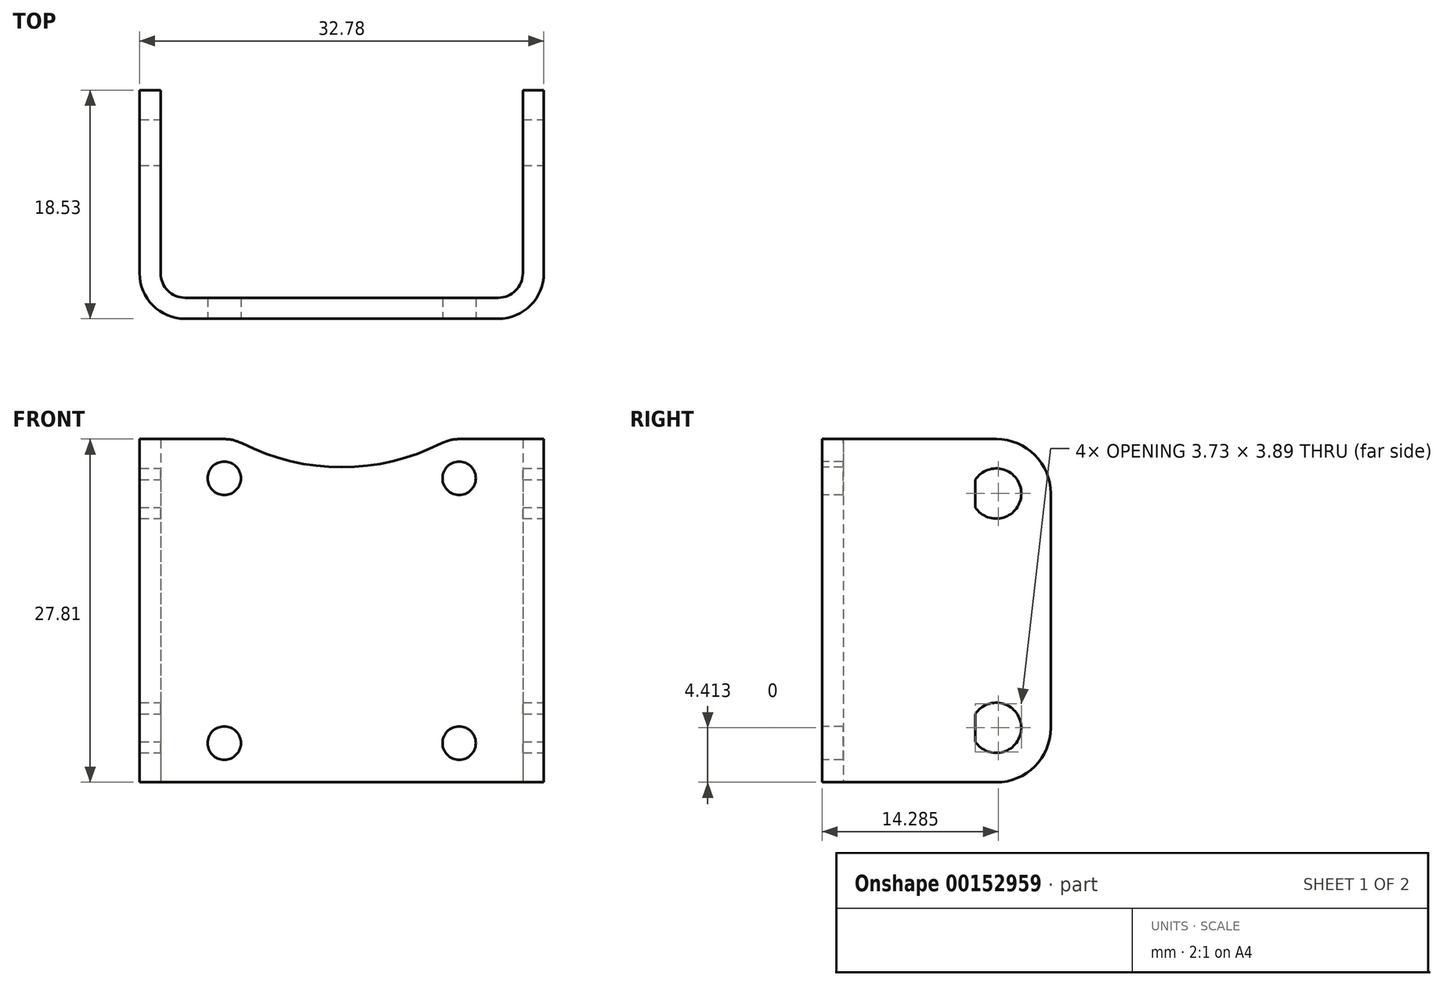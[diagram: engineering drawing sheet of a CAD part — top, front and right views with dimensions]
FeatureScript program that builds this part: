
annotation { "Feature Type Name" : "Feature", "Feature Type Description" : "" }
export const myFeature = defineFeature(function(context is Context, id is Id, definition is map)
    precondition{}
    {
        {
            var Q0;
            Q0=qCreatedBy(makeId("Top.planeOp"),FACE);
            var sketch = newSketch(context, id + "F0", { "sketchPlane" : qUnion([Q0])});
            skLineSegment(sketch, "E0.bottom", {"start": v(0, 0) * mm, "end": v(-29.36, 0) * mm});
            skLineSegment(sketch, "E0.top", {"start": v(1.7, -1.7) * mm, "end": v(-31.07, -1.7) * mm});
            skLineSegment(sketch, "E1.top", {"start": v(-29.36, 16.82) * mm, "end": v(-31.07, 16.82) * mm});
            skLineSegment(sketch, "E1.left", {"start": v(-29.36, 0) * mm, "end": v(-29.36, 16.82) * mm});
            skLineSegment(sketch, "E1.right", {"start": v(-31.07, -1.7) * mm, "end": v(-31.07, 16.82) * mm});
            skLineSegment(sketch, "E2.top", {"start": v(0, 16.82) * mm, "end": v(1.7, 16.82) * mm});
            skLineSegment(sketch, "E2.left", {"start": v(0, 0) * mm, "end": v(0, 16.82) * mm});
            skLineSegment(sketch, "E2.right", {"start": v(1.7, -1.7) * mm, "end": v(1.7, 16.82) * mm});
            skLineSegment(sketch, "E3", {"start": v(-14.68, 0) * mm, "end": v(-14.68, -1.7) * mm, "construction": true});
            skArc(sketch, "E4", {"start": v(-1.98, 0) * mm, "mid": v(-0.58, 0.58) * mm, "end": v(0, 1.98) * mm, "construction": true});
            skSolve(sketch);
        }
        {
            var Q0;
            Q0=qSketchRegion(id+"F0",true);
            extrude(context, id + "F1", {"entities" : qUnion([Q0]), "depth" : 27.8 * mm});
        }
        {
            var Q0;
            Q0=makeQuery(id+"F1.opExtrude","SWEPT_EDGE",EDGE,{"disambiguationData":[OSD([sQuery(id+"F0.wireOp",EDGE,"E0.top"),sQuery(id+"F0.wireOp",EDGE,"E2.right")])]});
            var Q1;
            Q1=makeQuery(id+"F1.opExtrude","SWEPT_EDGE",EDGE,{"disambiguationData":[OSD([sQuery(id+"F0.wireOp",EDGE,"E0.top"),sQuery(id+"F0.wireOp",EDGE,"E1.right")])]});
            var Q2;
            Q2=makeQuery(id+"FqNnmMD7oaRdpTN_1.opExtrude","CAP_EDGE",EDGE,{"disambiguationData":[OSD([sQuery(id+"FY5sMr6MULj5lJw_1.wireOp",EDGE,"W42EfhJi-fDm4-L9BW-folL-irsYfDskuzBk.top")])],"isStart":false});
            fillet(context, id + "F2", {"entities" : qUnion([Q0, Q1, Q2]), "radius" : 3.7 * mm, "tangentPropagation" : true, "allowEdgeOverflow" : false});
        }
        {
            var Q0;
            Q0=makeQuery(id+"F1.opExtrude","SWEPT_EDGE",EDGE,{"disambiguationData":[OSD([sQuery(id+"F0.wireOp",EDGE,"E0.bottom"),sQuery(id+"F0.wireOp",EDGE,"E2.left")])]});
            var Q1;
            Q1=makeQuery(id+"F1.opExtrude","SWEPT_EDGE",EDGE,{"disambiguationData":[OSD([sQuery(id+"F0.wireOp",EDGE,"E0.bottom"),sQuery(id+"F0.wireOp",EDGE,"E1.left")])]});
            fillet(context, id + "F3", {"entities" : qUnion([Q0, Q1]), "radius" : 1.98 * mm, "tangentPropagation" : true, "allowEdgeOverflow" : false});
        }
        {
            var Q0;
            Q0=makeQuery(id+"F1.opExtrude","SWEPT_FACE",FACE,{"disambiguationData":[OSD([sQuery(id+"F0.wireOp",EDGE,"E2.right")])]});
            var sketch = newSketch(context, id + "F4", { "sketchPlane" : qUnion([Q0])});
            skArc(sketch, "E5", {"start": v(10.71, 22.28) * mm, "mid": v(14.44, 23.4) * mm, "end": v(10.71, 24.52) * mm});
            skLineSegment(sketch, "E6", {"start": v(10.71, 22.28) * mm, "end": v(10.71, 24.52) * mm});
            skCircle(sketch, "E7", {"center": v(12.4, 23.4) * mm, "radius": 0.9 * mm, "construction": true});
            skArc(sketch, "E8", {"start": v(10.71, 3.3) * mm, "mid": v(14.44, 4.41) * mm, "end": v(10.71, 5.54) * mm});
            skLineSegment(sketch, "E9", {"start": v(10.71, 3.3) * mm, "end": v(10.71, 5.54) * mm});
            skLineSegment(sketch, "E10", {"start": v(12.4, 23.4) * mm, "end": v(11.5, 23.4) * mm, "construction": true});
            skLineSegment(sketch, "E11", {"start": v(12.4, 23.4) * mm, "end": v(12.4, 22.5) * mm, "construction": true});
            skLineSegment(sketch, "E12", {"start": v(11.5, 23.4) * mm, "end": v(10.71, 23.4) * mm, "construction": true});
            skLineSegment(sketch, "E13", {"start": v(12.4, 22.5) * mm, "end": v(12.4, 21.37) * mm, "construction": true});
            skLineSegment(sketch, "E14", {"start": v(12.4, 23.4) * mm, "end": v(12.4, 27.81) * mm, "construction": true});
            skLineSegment(sketch, "E15.bottom", {"start": v(12.4, 0) * mm, "end": v(16.82, 0) * mm, "construction": true});
            skLineSegment(sketch, "E15.top", {"start": v(12.4, 4.41) * mm, "end": v(16.82, 4.41) * mm, "construction": true});
            skLineSegment(sketch, "E15.left", {"start": v(12.4, 0) * mm, "end": v(12.4, 4.41) * mm, "construction": true});
            skLineSegment(sketch, "E15.right", {"start": v(16.82, 0) * mm, "end": v(16.82, 4.41) * mm, "construction": true});
            skSolve(sketch);
        }
        {
            var Q0;
            Q0=qSketchRegion(id+"F4",true);
            var Q1;
            Q1=makeQuery(id+"F1.opExtrude","SWEPT_FACE",FACE,{"disambiguationData":[OSD([sQuery(id+"F0.wireOp",EDGE,"E1.right")])]});
            extrude(context, id + "F5", {"entities" : qUnion([Q0]), "operationType" : NewBodyOperationType.REMOVE, "endBound" : BoundingType.UP_TO_SURFACE, "oppositeDirection" : true, "endBoundEntityFace" : qUnion([Q1]), "depth" : 25.4 * mm});
        }
        {
            var Q0;
            Q0=makeQuery(id+"F1.opExtrude","SWEPT_FACE",FACE,{"disambiguationData":[OSD([sQuery(id+"F0.wireOp",EDGE,"E0.top")])]});
            var sketch = newSketch(context, id + "F6", { "sketchPlane" : qUnion([Q0])});
            skArc(sketch, "E16", {"start": v(-5.16, 27.81) * mm, "mid": v(-5.9, 27.73) * mm, "end": v(-6.6, 27.47) * mm});
            skArc(sketch, "E17", {"start": v(-22.77, 27.47) * mm, "mid": v(-23.46, 27.73) * mm, "end": v(-24.2, 27.81) * mm});
            skArc(sketch, "E18", {"start": v(-22.77, 27.47) * mm, "mid": v(-14.68, 25.53) * mm, "end": v(-6.6, 27.47) * mm});
            skLineSegment(sketch, "E19", {"start": v(-24.2, 27.81) * mm, "end": v(-5.16, 27.81) * mm});
            skCircle(sketch, "E20", {"center": v(-24.2, 24.64) * mm, "radius": 1.35 * mm});
            skCircle(sketch, "E21", {"center": v(-5.16, 24.64) * mm, "radius": 1.35 * mm});
            skLineSegment(sketch, "E22", {"start": v(-14.68, 0) * mm, "end": v(-14.68, 3.18) * mm, "construction": true});
            skLineSegment(sketch, "E23", {"start": v(-24.2, 3.18) * mm, "end": v(-5.16, 3.18) * mm, "construction": true});
            skLineSegment(sketch, "E24", {"start": v(-5.16, 3.18) * mm, "end": v(-1.98, 3.18) * mm, "construction": true});
            skCircle(sketch, "E25", {"center": v(-24.2, 3.18) * mm, "radius": 1.35 * mm});
            skCircle(sketch, "E26", {"center": v(-5.16, 3.18) * mm, "radius": 1.35 * mm});
            skSolve(sketch);
        }
        {
            var Q0;
            Q0 = qSketchRegion(id + "F6", true);
            var Q1;
            Q1=makeQuery(id+"F1.opExtrude","SWEPT_FACE",FACE,{"disambiguationData":[OSD([sQuery(id+"F0.wireOp",EDGE,"E0.bottom")])]});
            extrude(context, id + "F7", {"entities" : qUnion([Q0]), "operationType" : NewBodyOperationType.REMOVE, "endBound" : BoundingType.UP_TO_SURFACE, "oppositeDirection" : true, "endBoundEntityFace" : qUnion([Q1]), "depth" : 25.4 * mm});
        }
        {
            var Q0;
            Q0=makeQuery(id+"F1.opExtrude","CAP_EDGE",EDGE,{"disambiguationData":[OSD([sQuery(id+"F0.wireOp",EDGE,"E2.top")])],"isStart":false});
            var Q1;
            Q1=makeQuery(id+"F1.opExtrude","CAP_EDGE",EDGE,{"disambiguationData":[OSD([sQuery(id+"F0.wireOp",EDGE,"E1.top")])],"isStart":false});
            var Q2;
            Q2=makeQuery(id+"F1.opExtrude","CAP_EDGE",EDGE,{"disambiguationData":[OSD([sQuery(id+"F0.wireOp",EDGE,"E2.top")])],"isStart":true});
            var Q3;
            Q3=makeQuery(id+"F1.opExtrude","CAP_EDGE",EDGE,{"disambiguationData":[OSD([sQuery(id+"F0.wireOp",EDGE,"E1.top")])],"isStart":true});
            fillet(context, id + "F8", {"entities" : qUnion([Q0, Q1, Q2, Q3]), "radius" : 4.4 * mm, "tangentPropagation" : true, "allowEdgeOverflow" : false});
        }
    });
